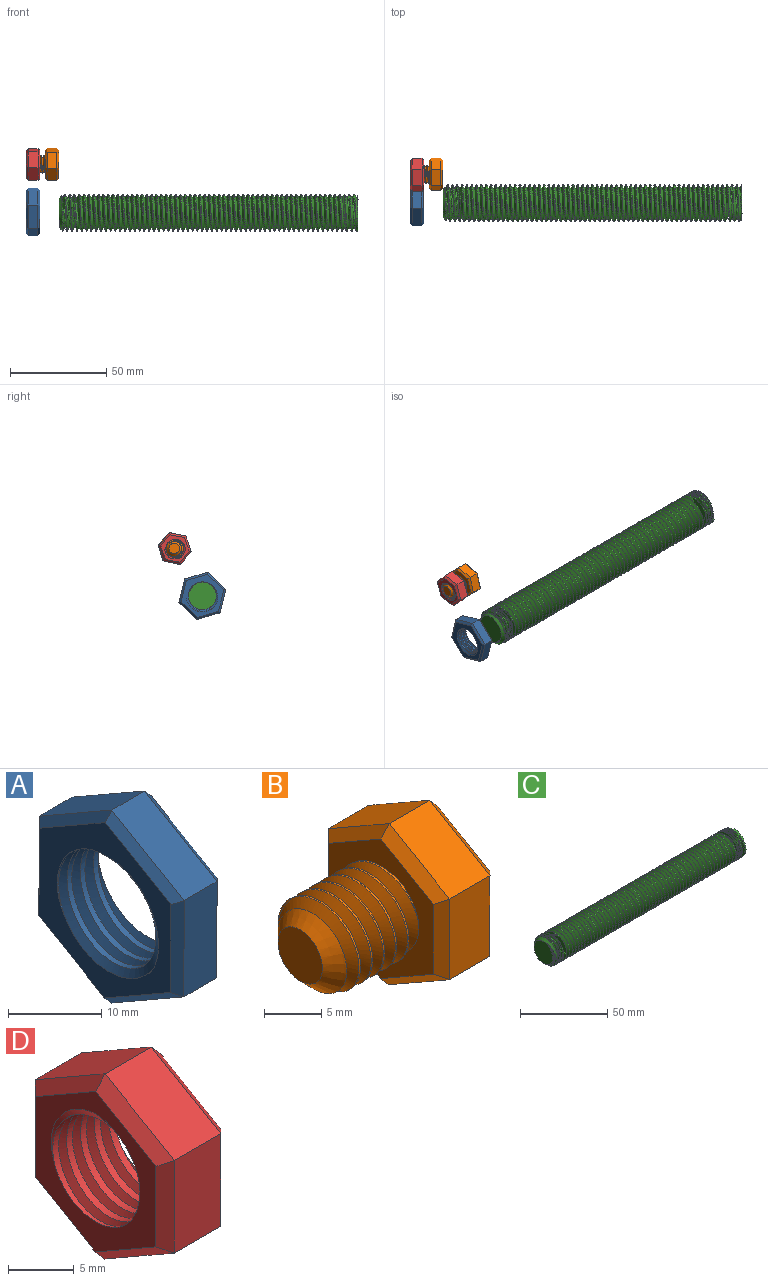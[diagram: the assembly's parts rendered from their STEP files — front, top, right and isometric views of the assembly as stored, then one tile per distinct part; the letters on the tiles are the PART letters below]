
ASSEMBLY  parts=4 mates=2
PART A: 23 faces, bbox 9.3x22.7x26 mm
  f0: cylinder r=7.24mm len=14.48mm, axis (1,0,0), area 111.6mm2, adj f7,f8,f21,f22
  f1: plane 10.98x6.38mm, normal (0,-0.5,0.86), area 63.5mm2, adj f2,f6,f14,f18
  f2: plane 12.7x5mm, normal (0,-1,0), area 63.5mm2, adj f1,f3,f12,f16
  f3: plane 11.02x6.32mm, normal (0,-0.5,-0.87), area 63.5mm2, adj f2,f4,f10,f15
  f4: plane 10.98x6.38mm, normal (0,0.5,-0.86), area 63.5mm2, adj f3,f5,f9,f17
  f5: plane 12.7x5mm, normal (0,1,0), area 63.5mm2, adj f4,f6,f11,f19
  f6: plane 11.02x6.32mm, normal (0,0.5,0.87), area 63.5mm2, adj f1,f5,f13,f20
  f7: plane 23.73x20.67mm, normal (-1,0,0), area 164.4mm2, adj f0,f9,f10,f11,f12,f13,f14,f21
  f8: plane 23.73x20.67mm, normal (1,0,0), area 164.4mm2, adj f0,f15,f16,f17,f18,f19,f20,f21
  f9: plane 10.99x6.96mm, normal (-0.71,0.36,-0.61), area 17.1mm2, adj f4,f7,f10,f11
  f10: plane 11.02x6.9mm, normal (-0.71,-0.35,-0.61), area 17.1mm2, adj f3,f7,f9,f12
  f11: plane 12.7x1.03mm, normal (-0.71,0.71,0), area 17.1mm2, adj f5,f7,f9,f13
  f12: plane 12.7x1.03mm, normal (-0.71,-0.71,0), area 17.1mm2, adj f2,f7,f10,f14
  f13: plane 11.02x6.9mm, normal (-0.71,0.35,0.61), area 17.1mm2, adj f6,f7,f11,f14
  f14: plane 10.99x6.96mm, normal (-0.71,-0.36,0.61), area 17.1mm2, adj f1,f7,f12,f13
  f15: plane 11.02x6.9mm, normal (0.71,-0.35,-0.61), area 17.1mm2, adj f3,f8,f16,f17
  f16: plane 12.7x1.03mm, normal (0.71,-0.71,0), area 17.1mm2, adj f2,f8,f15,f18
  f17: plane 10.99x6.96mm, normal (0.71,0.36,-0.61), area 17.1mm2, adj f4,f8,f15,f19
  f18: plane 10.99x6.96mm, normal (0.71,-0.36,0.61), area 17.1mm2, adj f1,f8,f16,f20
  f19: plane 12.7x1.03mm, normal (0.71,0.71,0), area 17.1mm2, adj f5,f8,f17,f20
  f20: plane 11.02x6.9mm, normal (0.71,0.35,0.61), area 17.1mm2, adj f6,f8,f18,f19
  f21: bspline ~19.31x16.73mm, area 223mm2, adj f0,f7,f8,f22
  f22: bspline ~19.31x16.73mm, area 223mm2, adj f0,f7,f8,f21
PART B: 25 faces, bbox 17.8x15.9x18.1 mm
  f0: cylinder r=4.75mm len=9.5mm, axis (1,0,0), area 28.1mm2, adj f1,f2,f4,f12
  f1: bspline ~10.97x9.91mm, area 196.7mm2, adj f0,f2,f4,f12
  f2: bspline ~10.97x10.66mm, area 196.6mm2, adj f0,f1,f4,f12
  f3: plane 5.5x5.5mm, normal (-1,0,0), area 23.8mm2, adj f4
  f4: cone r=4.75mm half-angle=45deg, axis (1,0,0), area 47.4mm2, adj f0,f1,f2,f3
  f5: plane 7.48x5mm, normal (0,-0.5,0.86), area 43.3mm2, adj f6,f10,f18,f22
  f6: plane 8.66x5mm, normal (0,-1,0), area 43.3mm2, adj f5,f7,f16,f20
  f7: plane 7.52x5mm, normal (0,-0.5,-0.87), area 43.3mm2, adj f6,f8,f14,f19
  f8: plane 7.48x5mm, normal (0,0.5,-0.86), area 43.3mm2, adj f7,f9,f13,f21
  f9: plane 8.66x5mm, normal (0,1,0), area 43.3mm2, adj f8,f10,f15,f23
  f10: plane 7.52x5mm, normal (0,0.5,0.87), area 43.3mm2, adj f5,f9,f17,f24
  f11: plane 15.01x13.03mm, normal (1,0,0), area 146.4mm2, adj f13,f14,f15,f16,f17,f18
  f12: plane 15.83x13.85mm, normal (-1,0,0), area 89.2mm2, adj f0,f1,f2,f19,f20,f21,f22,f23
  f13: plane 7.49x4.93mm, normal (0.71,0.36,-0.61), area 11.4mm2, adj f8,f11,f14,f15
  f14: plane 7.52x4.88mm, normal (0.71,-0.35,-0.61), area 11.4mm2, adj f7,f11,f13,f16
  f15: plane 8.66x1.03mm, normal (0.71,0.71,0), area 11.4mm2, adj f9,f11,f13,f17
  f16: plane 8.66x1.03mm, normal (0.71,-0.71,0), area 11.4mm2, adj f6,f11,f14,f18
  f17: plane 7.52x4.88mm, normal (0.71,0.35,0.61), area 11.4mm2, adj f10,f11,f15,f18
  f18: plane 7.49x4.93mm, normal (0.71,-0.36,0.61), area 11.4mm2, adj f5,f11,f16,f17
  f19: plane 7.52x4.88mm, normal (-0.71,-0.35,-0.61), area 11.4mm2, adj f7,f12,f20,f21
  f20: plane 8.66x1.03mm, normal (-0.71,-0.71,0), area 11.4mm2, adj f6,f12,f19,f22
  f21: plane 7.49x4.93mm, normal (-0.71,0.36,-0.61), area 11.4mm2, adj f8,f12,f19,f23
  f22: plane 7.49x4.93mm, normal (-0.71,-0.36,0.61), area 11.4mm2, adj f5,f12,f20,f24
  f23: plane 8.66x1.03mm, normal (-0.71,0.71,0), area 11.4mm2, adj f9,f12,f21,f24
  f24: plane 7.52x4.88mm, normal (-0.71,0.35,0.61), area 11.4mm2, adj f10,f12,f22,f23
PART C: 7 faces, bbox 158.6x23.6x20.6 mm
  f0: cylinder r=9.6mm len=153mm, axis (1,0,0), area 567.9mm2, adj f2,f3,f4,f5,f6
  f1: plane 15.2x15.2mm, normal (-1,0,0), area 181.5mm2, adj f3
  f2: plane 20.59x19.82mm, normal (1,0,0), area 266.1mm2, adj f0,f4,f5
  f3: cone r=9.6mm half-angle=45deg, axis (1,0,0), area 86.9mm2, adj f0,f1,f5,f6
  f4: plane 1.89x1.09mm, normal (0,1,0), area 1mm2, adj f0,f2,f6
  f5: bspline ~156.09x22.17mm, area 7304mm2, adj f0,f2,f3,f6
  f6: bspline ~156.09x22.17mm, area 7321.7mm2, adj f0,f3,f4,f5
PART D: 23 faces, bbox 9.1x15.4x17.7 mm
  f0: plane 7.49x5mm, normal (0,-0.5,0.86), area 43.3mm2, adj f1,f5,f13,f17
  f1: plane 8.66x5mm, normal (0,-1,0), area 43.3mm2, adj f0,f2,f11,f15
  f2: plane 7.51x5mm, normal (0,-0.5,-0.87), area 43.3mm2, adj f1,f3,f9,f14
  f3: plane 7.49x5mm, normal (0,0.5,-0.86), area 43.3mm2, adj f2,f4,f8,f16
  f4: plane 8.66x5mm, normal (0,1,0), area 43.3mm2, adj f3,f5,f10,f18
  f5: plane 7.51x5mm, normal (0,0.5,0.87), area 43.3mm2, adj f0,f4,f12,f19
  f6: plane 15.37x13.38mm, normal (-1,0,0), area 71.4mm2, adj f8,f9,f10,f11,f12,f13,f20,f21
  f7: plane 15.37x13.38mm, normal (1,0,0), area 71.4mm2, adj f14,f15,f16,f17,f18,f19,f20,f21
  f8: plane 7.49x4.93mm, normal (-0.71,0.36,-0.61), area 11.4mm2, adj f3,f6,f9,f10
  f9: plane 7.51x4.89mm, normal (-0.71,-0.35,-0.61), area 11.4mm2, adj f2,f6,f8,f11
  f10: plane 8.66x1.02mm, normal (-0.71,0.71,0), area 11.4mm2, adj f4,f6,f8,f12
  f11: plane 8.66x1.02mm, normal (-0.71,-0.71,0), area 11.4mm2, adj f1,f6,f9,f13
  f12: plane 7.51x4.89mm, normal (-0.71,0.35,0.61), area 11.4mm2, adj f5,f6,f10,f13
  f13: plane 7.49x4.93mm, normal (-0.71,-0.36,0.61), area 11.4mm2, adj f0,f6,f11,f12
  f14: plane 7.51x4.89mm, normal (0.71,-0.35,-0.61), area 11.4mm2, adj f2,f7,f15,f16
  f15: plane 8.66x1.02mm, normal (0.71,-0.71,0), area 11.4mm2, adj f1,f7,f14,f17
  f16: plane 7.49x4.93mm, normal (0.71,0.36,-0.61), area 11.4mm2, adj f3,f7,f14,f18
  f17: plane 7.49x4.93mm, normal (0.71,-0.36,0.61), area 11.4mm2, adj f0,f7,f15,f19
  f18: plane 8.66x1.02mm, normal (0.71,0.71,0), area 11.4mm2, adj f4,f7,f16,f19
  f19: plane 7.51x4.89mm, normal (0.71,0.35,0.61), area 11.4mm2, adj f5,f7,f17,f18
  f20: cylinder r=4.66mm len=9.32mm, axis (1,0,0), area 85.4mm2, adj f6,f7,f21,f22
  f21: bspline ~12.5x10.82mm, area 128.4mm2, adj f6,f7,f20,f22
  f22: bspline ~12.5x10.82mm, area 128.5mm2, adj f6,f7,f20,f21
PLACE A rot(axis=(0,0.6,-0.8),180deg) t=(-55.27,-6.86,23.48)mm fixed
PLACE B rot(axis=(1,0,0),103.9deg) t=(-41.91,7.73,48.08)mm
PLACE C rot(axis=(1,0,0),109.9deg) t=(116.73,-7.25,23.06)mm
PLACE D rot(axis=(1,0,0),100.2deg) t=(-48.16,7.38,48.02)mm fixed
MATE cylindrical C.f0 <-> A.f7  axis (-1,0,0) through (-38.27,-7.25,23.06)mm
MATE cylindrical B.f0 <-> D.f6  axis (-1,0,0) through (-55.41,7.73,48.08)mm
